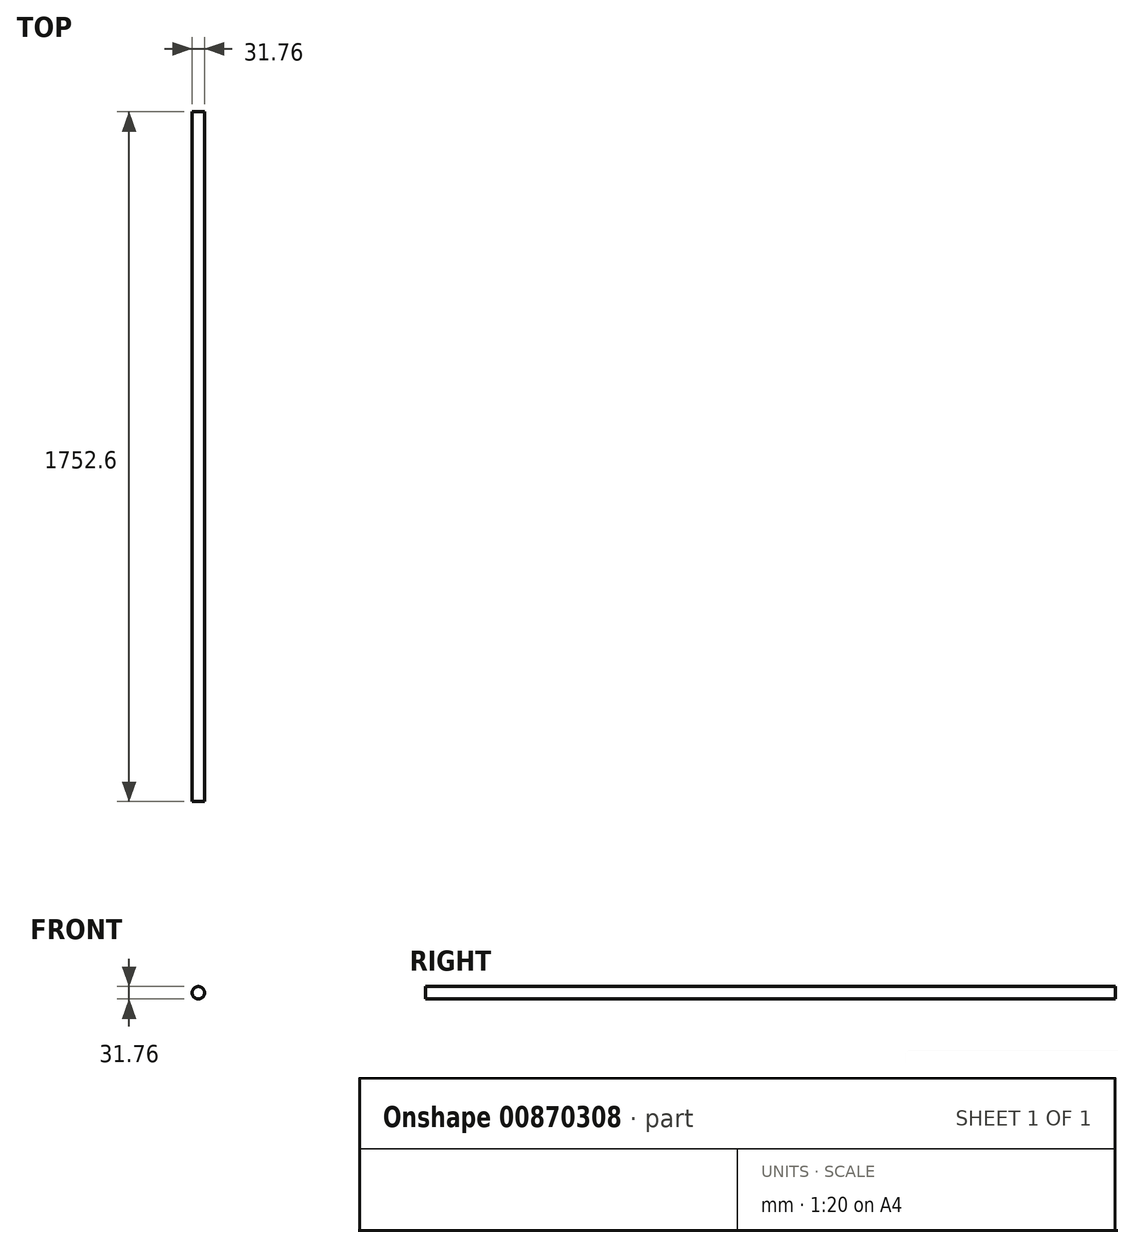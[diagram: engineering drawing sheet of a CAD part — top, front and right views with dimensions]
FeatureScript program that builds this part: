
annotation { "Feature Type Name" : "Feature", "Feature Type Description" : "" }
export const myFeature = defineFeature(function(context is Context, id is Id, definition is map)
    precondition{}
    {
        {
            var Q0;
            Q0=qCreatedBy(makeId("Front.planeOp"),FACE);
            var sketch = newSketch(context, id + "F0", { "sketchPlane" : qUnion([Q0])});
            skCircle(sketch, "E0", {"center": v(0, 0) * mm, "radius": 15.88 * mm});
            skSolve(sketch);
        }
        {
            var Q0;
            Q0=makeQuery(id+"F0.imprint","IMPRINT",FACE,{"disambiguationData":[TD([[makeQuery(id+"F0.imprint","IMPRINT",EDGE,{"derivedFrom":sQuery(id+"F0.wireOp",EDGE,"E0")}),1.0]])]});
            extrude(context, id + "F1", {"entities" : qUnion([Q0]), "depth" : 1752.6 * mm, "offsetDistance" : 25.4 * mm});
        }
    });
